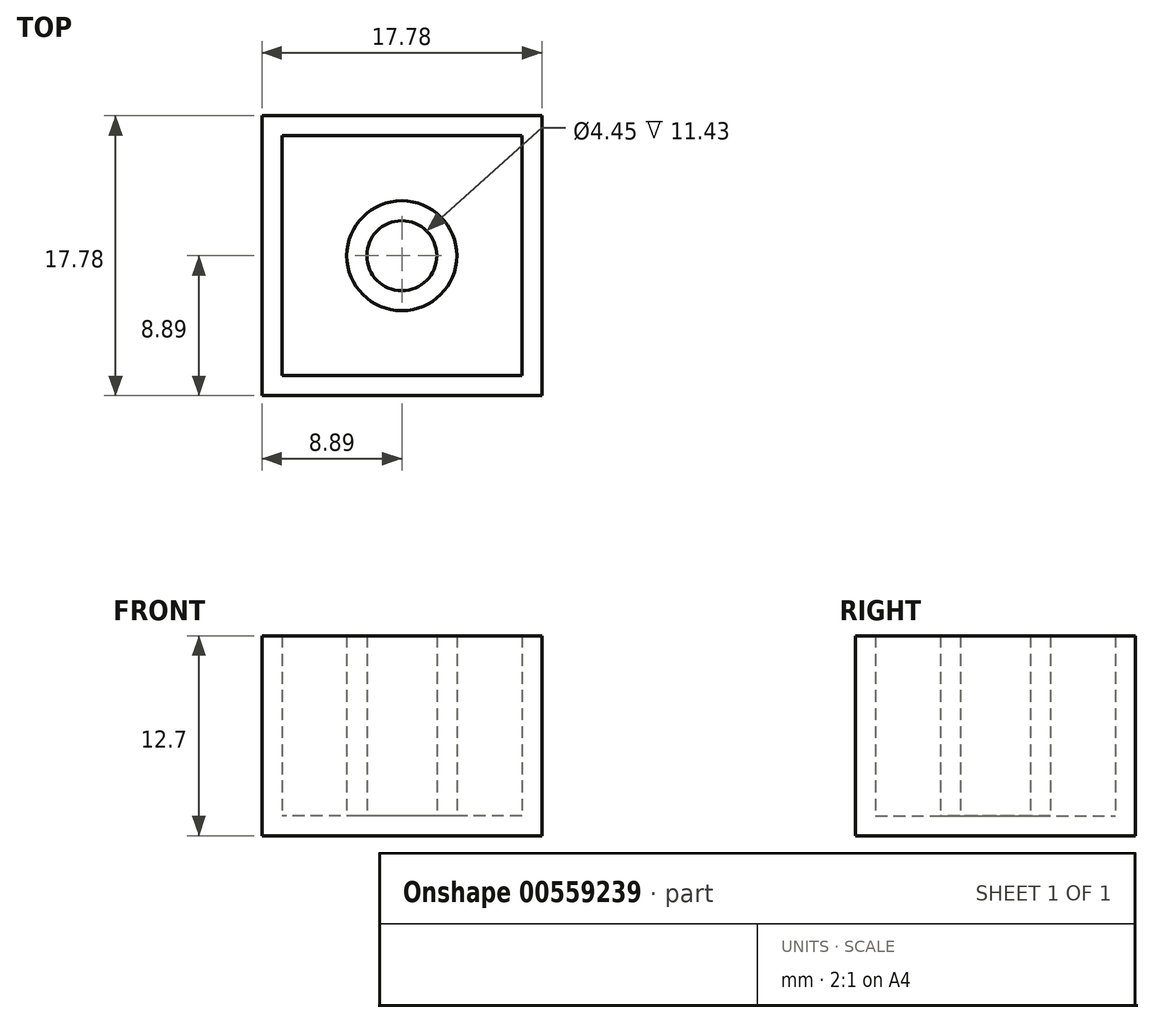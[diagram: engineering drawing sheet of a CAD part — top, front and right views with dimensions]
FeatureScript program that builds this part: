
annotation { "Feature Type Name" : "Feature", "Feature Type Description" : "" }
export const myFeature = defineFeature(function(context is Context, id is Id, definition is map)
    precondition{}
    {
        {
            var Q0;
            Q0=qCreatedBy(makeId("Top.planeOp"),FACE);
            var sketch = newSketch(context, id + "F0", { "sketchPlane" : qUnion([Q0])});
            skLineSegment(sketch, "E0.bottom", {"start": v(7.62, -7.62) * mm, "end": v(-7.62, -7.62) * mm});
            skLineSegment(sketch, "E0.top", {"start": v(7.62, 7.62) * mm, "end": v(-7.62, 7.62) * mm});
            skLineSegment(sketch, "E0.left", {"start": v(7.62, -7.62) * mm, "end": v(7.62, 7.62) * mm});
            skLineSegment(sketch, "E0.right", {"start": v(-7.62, -7.62) * mm, "end": v(-7.62, 7.62) * mm});
            skPoint(sketch, "E0.middle", {"position": v(0, 0) * mm});
            skLineSegment(sketch, "E1.0", {"start": v(8.9, 8.9) * mm, "end": v(-8.9, 8.9) * mm});
            skLineSegment(sketch, "E1.1", {"start": v(8.9, -8.9) * mm, "end": v(8.9, 8.9) * mm});
            skLineSegment(sketch, "E1.2", {"start": v(8.9, -8.9) * mm, "end": v(-8.89, -8.9) * mm});
            skLineSegment(sketch, "E1.3", {"start": v(-8.89, -8.9) * mm, "end": v(-8.9, 8.9) * mm});
            skCircle(sketch, "E2", {"center": v(0, 0) * mm, "radius": 2.22 * mm});
            skCircle(sketch, "E3.0", {"center": v(0, 0) * mm, "radius": 3.5 * mm});
            skSolve(sketch);
        }
        {
            var Q0;
            Q0=makeQuery(id+"F0.imprint","IMPRINT",FACE,{"disambiguationData":[TD([[makeQuery(id+"F0.imprint","IMPRINT",EDGE,{"derivedFrom":sQuery(id+"F0.wireOp",EDGE,"E0.bottom")}),-1.0]])]});
            var Q1;
            Q1=makeQuery(id+"F0.imprint","IMPRINT",FACE,{"disambiguationData":[TD([[makeQuery(id+"F0.imprint","IMPRINT",EDGE,{"derivedFrom":sQuery(id+"F0.wireOp",EDGE,"E2")}),1.0]])]});
            var Q2;
            Q2=makeQuery(id+"F0.imprint","IMPRINT",FACE,{"disambiguationData":[TD([[makeQuery(id+"F0.imprint","IMPRINT",EDGE,{"derivedFrom":sQuery(id+"F0.wireOp",EDGE,"E2")}),-1.0]])]});
            extrude(context, id + "F1", {"entities" : qUnion([Q0, Q1, Q2]), "depth" : 1.27 * mm, "offsetDistance" : 25.4 * mm});
        }
        {
            var Q0;
            Q0=makeQuery(id+"F0.imprint","IMPRINT",FACE,{"disambiguationData":[TD([[makeQuery(id+"F0.imprint","IMPRINT",EDGE,{"derivedFrom":sQuery(id+"F0.wireOp",EDGE,"E0.bottom")}),1.0]])]});
            extrude(context, id + "F2", {"entities" : qUnion([Q0]), "operationType" : NewBodyOperationType.ADD, "depth" : 12.7 * mm, "offsetDistance" : 25.4 * mm});
        }
        {
            var Q0;
            Q0=makeQuery(id+"F0.imprint","IMPRINT",FACE,{"disambiguationData":[TD([[makeQuery(id+"F0.imprint","IMPRINT",EDGE,{"derivedFrom":sQuery(id+"F0.wireOp",EDGE,"E2")}),-1.0]])]});
            extrude(context, id + "F3", {"entities" : qUnion([Q0]), "operationType" : NewBodyOperationType.ADD, "depth" : 12.7 * mm, "offsetDistance" : 25.4 * mm});
        }
    });
